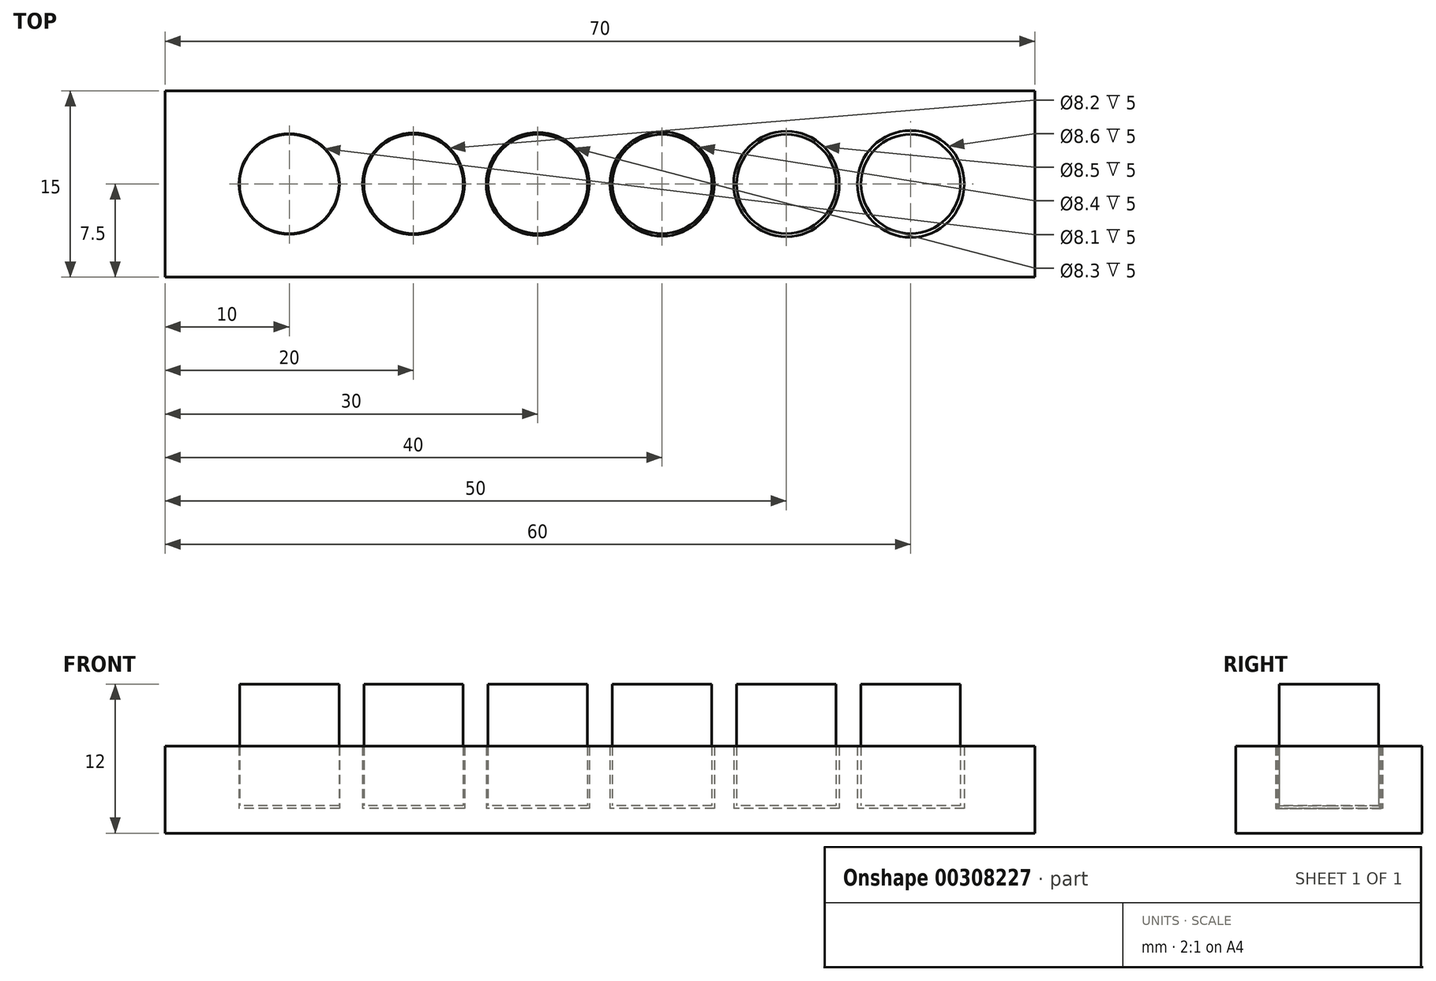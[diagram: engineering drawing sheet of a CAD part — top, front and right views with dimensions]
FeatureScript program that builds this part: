
annotation { "Feature Type Name" : "Feature", "Feature Type Description" : "" }
export const myFeature = defineFeature(function(context is Context, id is Id, definition is map)
    precondition{}
    {
        {
            var Q0;
            Q0=qCreatedBy(makeId("Top.planeOp"),FACE);
            var sketch = newSketch(context, id + "F0", { "sketchPlane" : qUnion([Q0])});
            skLineSegment(sketch, "E0.bottom", {"start": v(35, 7.5) * mm, "end": v(-35, 7.5) * mm});
            skLineSegment(sketch, "E0.top", {"start": v(35, -7.5) * mm, "end": v(-35, -7.5) * mm});
            skLineSegment(sketch, "E0.left", {"start": v(35, 7.5) * mm, "end": v(35, -7.5) * mm});
            skLineSegment(sketch, "E0.right", {"start": v(-35, 7.5) * mm, "end": v(-35, -7.5) * mm});
            skPoint(sketch, "E0.middle", {"position": v(0, 0) * mm});
            skCircle(sketch, "E1", {"center": v(-25, 0) * mm, "radius": 4.05 * mm});
            skCircle(sketch, "E2", {"center": v(5, 0) * mm, "radius": 4.2 * mm});
            skCircle(sketch, "E3", {"center": v(15, 0) * mm, "radius": 4.25 * mm});
            skCircle(sketch, "E4", {"center": v(25, 0) * mm, "radius": 4.3 * mm});
            skCircle(sketch, "E5", {"center": v(-15, 0) * mm, "radius": 4.1 * mm});
            skCircle(sketch, "E6", {"center": v(-5, 0) * mm, "radius": 4.15 * mm});
            skLineSegment(sketch, "E7", {"start": v(-35, 0) * mm, "end": v(-25, 0) * mm, "construction": true});
            skLineSegment(sketch, "E8", {"start": v(-15, 0) * mm, "end": v(-5, 0) * mm, "construction": true});
            skLineSegment(sketch, "E9", {"start": v(-5, 0) * mm, "end": v(5, 0) * mm, "construction": true});
            skLineSegment(sketch, "E10", {"start": v(15, 0) * mm, "end": v(5, 0) * mm, "construction": true});
            skLineSegment(sketch, "E11", {"start": v(15, 0) * mm, "end": v(25, 0) * mm, "construction": true});
            skLineSegment(sketch, "E12", {"start": v(-15, 0) * mm, "end": v(-25, 0) * mm, "construction": true});
            skLineSegment(sketch, "E13", {"start": v(25, 0) * mm, "end": v(35, 0) * mm, "construction": true});
            skSolve(sketch);
        }
        {
            var Q0;
            Q0=qSketchRegion(id+"F0",true);
            extrude(context, id + "F1", {"entities" : qUnion([Q0]), "depth" : 7 * mm});
        }
        {
            var Q0;
            Q0=makeQuery(id+"F0.imprint","IMPRINT",FACE,{"disambiguationData":[TD([[makeQuery(id+"F0.imprint","IMPRINT",EDGE,{"derivedFrom":sQuery(id+"F0.wireOp",EDGE,"E1")}),1.0]])]});
            var Q1;
            Q1=makeQuery(id+"F0.imprint","IMPRINT",FACE,{"disambiguationData":[TD([[makeQuery(id+"F0.imprint","IMPRINT",EDGE,{"derivedFrom":sQuery(id+"F0.wireOp",EDGE,"E5")}),1.0]])]});
            var Q2;
            Q2=makeQuery(id+"F0.imprint","IMPRINT",FACE,{"disambiguationData":[TD([[makeQuery(id+"F0.imprint","IMPRINT",EDGE,{"derivedFrom":sQuery(id+"F0.wireOp",EDGE,"E6")}),1.0]])]});
            var Q3;
            Q3=makeQuery(id+"F0.imprint","IMPRINT",FACE,{"disambiguationData":[TD([[makeQuery(id+"F0.imprint","IMPRINT",EDGE,{"derivedFrom":sQuery(id+"F0.wireOp",EDGE,"E2")}),1.0]])]});
            var Q4;
            Q4=makeQuery(id+"F0.imprint","IMPRINT",FACE,{"disambiguationData":[TD([[makeQuery(id+"F0.imprint","IMPRINT",EDGE,{"derivedFrom":sQuery(id+"F0.wireOp",EDGE,"E3")}),1.0]])]});
            var Q5;
            Q5=makeQuery(id+"F0.imprint","IMPRINT",FACE,{"disambiguationData":[TD([[makeQuery(id+"F0.imprint","IMPRINT",EDGE,{"derivedFrom":sQuery(id+"F0.wireOp",EDGE,"E4")}),1.0]])]});
            extrude(context, id + "F2", {"entities" : qUnion([Q0, Q1, Q2, Q3, Q4, Q5]), "operationType" : NewBodyOperationType.ADD, "depth" : 2 * mm});
        }
        {
            var Q0;
            Q0=makeQuery(id+"F1.opExtrude","CAP_FACE",FACE,{"disambiguationData":[OSD([sQuery(id+"F0.wireOp",EDGE,"E0.bottom"),sQuery(id+"F0.wireOp",EDGE,"E0.top"),sQuery(id+"F0.wireOp",EDGE,"E0.left"),sQuery(id+"F0.wireOp",EDGE,"E0.right"),sQuery(id+"F0.wireOp",EDGE,"E1"),sQuery(id+"F0.wireOp",EDGE,"E2"),sQuery(id+"F0.wireOp",EDGE,"E3"),sQuery(id+"F0.wireOp",EDGE,"E4"),sQuery(id+"F0.wireOp",EDGE,"E5"),sQuery(id+"F0.wireOp",EDGE,"E6")])],"isStart":false});
            var sketch = newSketch(context, id + "F3", { "sketchPlane" : qUnion([Q0])});
            skLineSegment(sketch, "E14.0.0", {"start": v(-35, -7.5) * mm, "end": v(35, -7.5) * mm});
            skLineSegment(sketch, "E14.0.1", {"start": v(35, -7.5) * mm, "end": v(35, 7.5) * mm});
            skLineSegment(sketch, "E14.0.2", {"start": v(35, 7.5) * mm, "end": v(-35, 7.5) * mm});
            skLineSegment(sketch, "E14.0.3", {"start": v(-35, 7.5) * mm, "end": v(-35, -7.5) * mm});
            skCircle(sketch, "E15", {"center": v(-25, 0) * mm, "radius": 4 * mm});
            skCircle(sketch, "E16", {"center": v(-15, 0) * mm, "radius": 4 * mm});
            skCircle(sketch, "E17", {"center": v(-5, 0) * mm, "radius": 4 * mm});
            skCircle(sketch, "E18", {"center": v(5, 0) * mm, "radius": 4 * mm});
            skCircle(sketch, "E19", {"center": v(15, 0) * mm, "radius": 4 * mm});
            skCircle(sketch, "E20", {"center": v(25, 0) * mm, "radius": 4 * mm});
            skSolve(sketch);
        }
        {
            var Q0;
            Q0=makeQuery(id+"F3.imprint","IMPRINT",FACE,{"disambiguationData":[TD([[makeQuery(id+"F3.imprint","IMPRINT",EDGE,{"derivedFrom":sQuery(id+"F3.wireOp",EDGE,"E15")}),1.0]])]});
            var Q1;
            Q1=makeQuery(id+"F3.imprint","IMPRINT",FACE,{"disambiguationData":[TD([[makeQuery(id+"F3.imprint","IMPRINT",EDGE,{"derivedFrom":sQuery(id+"F3.wireOp",EDGE,"E16")}),1.0]])]});
            var Q2;
            Q2=makeQuery(id+"F3.imprint","IMPRINT",FACE,{"disambiguationData":[TD([[makeQuery(id+"F3.imprint","IMPRINT",EDGE,{"derivedFrom":sQuery(id+"F3.wireOp",EDGE,"E17")}),1.0]])]});
            var Q3;
            Q3=makeQuery(id+"F3.imprint","IMPRINT",FACE,{"disambiguationData":[TD([[makeQuery(id+"F3.imprint","IMPRINT",EDGE,{"derivedFrom":sQuery(id+"F3.wireOp",EDGE,"E18")}),1.0]])]});
            var Q4;
            Q4=makeQuery(id+"F3.imprint","IMPRINT",FACE,{"disambiguationData":[TD([[makeQuery(id+"F3.imprint","IMPRINT",EDGE,{"derivedFrom":sQuery(id+"F3.wireOp",EDGE,"E19")}),1.0]])]});
            var Q5;
            Q5=makeQuery(id+"F3.imprint","IMPRINT",FACE,{"disambiguationData":[TD([[makeQuery(id+"F3.imprint","IMPRINT",EDGE,{"derivedFrom":sQuery(id+"F3.wireOp",EDGE,"E20")}),1.0]])]});
            extrude(context, id + "F4", {"entities" : qUnion([Q0, Q1, Q2, Q3, Q4, Q5]), "depth" : 5 * mm, "hasSecondDirection" : true, "secondDirectionOppositeDirection" : true, "secondDirectionDepth" : 4.8 * mm});
        }
    });
